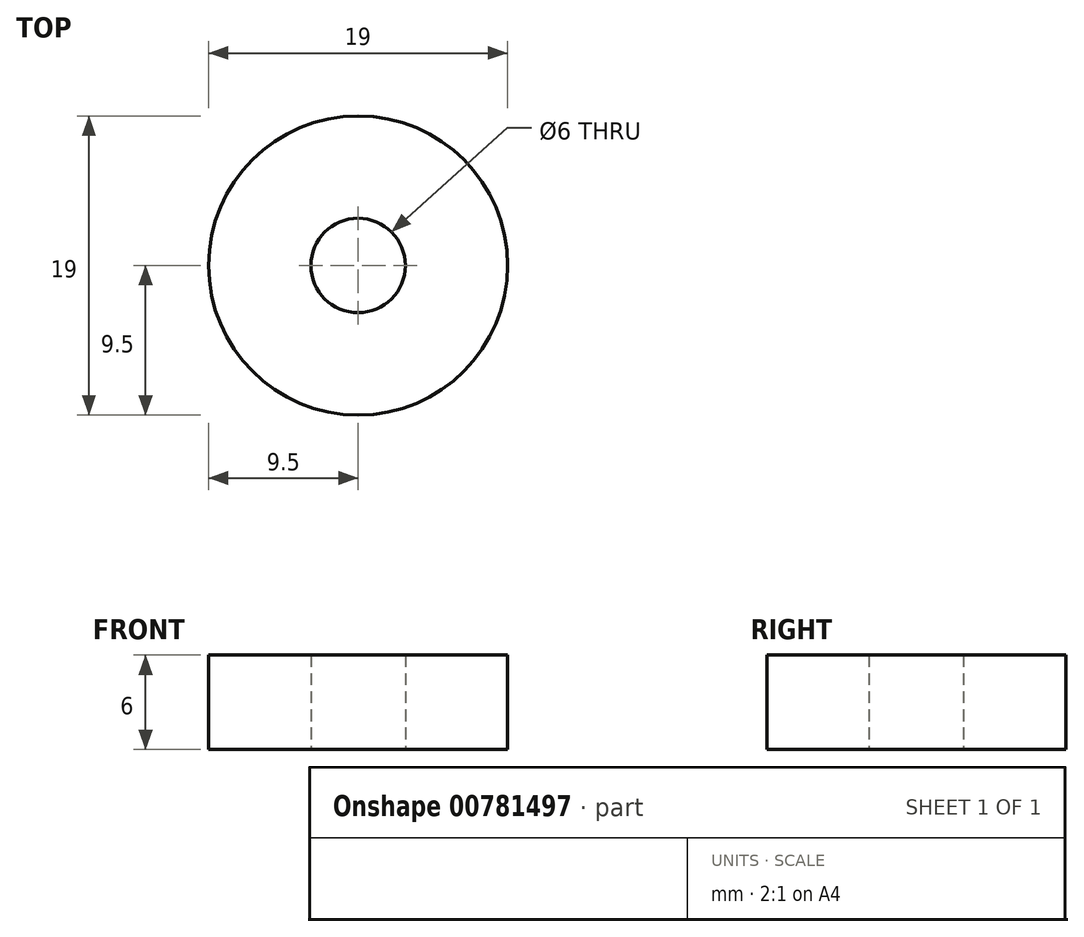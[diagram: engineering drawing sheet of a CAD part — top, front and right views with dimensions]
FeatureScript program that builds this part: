
annotation { "Feature Type Name" : "Feature", "Feature Type Description" : "" }
export const myFeature = defineFeature(function(context is Context, id is Id, definition is map)
    precondition{}
    {
        {
            var Q0;
            Q0=qCreatedBy(makeId("Top.planeOp"),FACE);
            var sketch = newSketch(context, id + "F0", { "sketchPlane" : qUnion([Q0])});
            skCircle(sketch, "E0", {"center": v(0, 0) * mm, "radius": 9.5 * mm});
            skSolve(sketch);
        }
        {
            var Q0;
            Q0=qCreatedBy(makeId("Top.planeOp"),FACE);
            var sketch = newSketch(context, id + "F1", { "sketchPlane" : qUnion([Q0])});
            skCircle(sketch, "E1", {"center": v(0, 0) * mm, "radius": 3 * mm});
            skSolve(sketch);
        }
        {
            var Q0;
            Q0=makeQuery(id+"F0.imprint","IMPRINT",FACE,{"disambiguationData":[TD([[makeQuery(id+"F0.imprint","IMPRINT",EDGE,{"derivedFrom":sQuery(id+"F0.wireOp",EDGE,"E0")}),1.0]])]});
            extrude(context, id + "F2", {"entities" : qUnion([Q0]), "depth" : 6 * mm, "offsetDistance" : 25.4 * mm});
        }
        {
            var Q0;
            Q0 = qSketchRegion(id + "F1", true);
            extrude(context, id + "F3", {"entities" : qUnion([Q0]), "operationType" : NewBodyOperationType.REMOVE, "depth" : 25.4 * mm, "offsetDistance" : 25.4 * mm});
        }
    });
